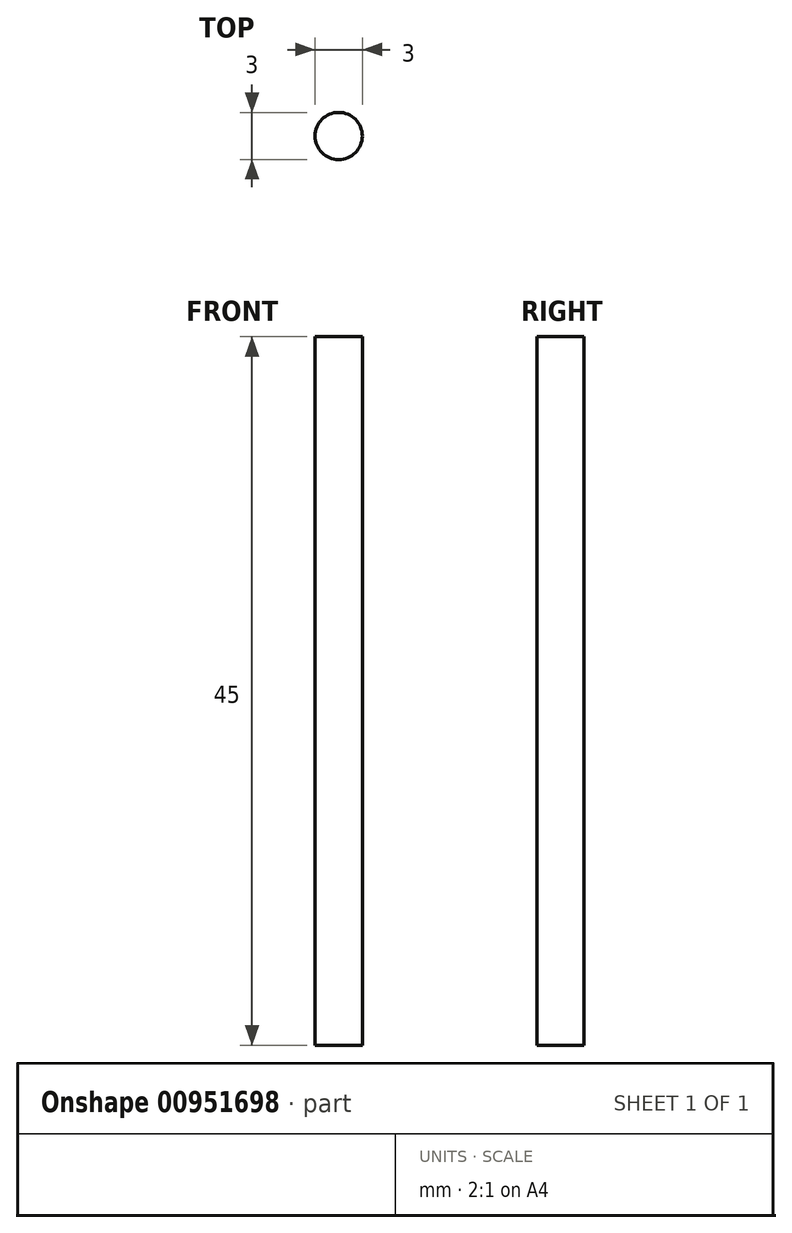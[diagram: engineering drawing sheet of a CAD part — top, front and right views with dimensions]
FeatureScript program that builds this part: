
annotation { "Feature Type Name" : "Feature", "Feature Type Description" : "" }
export const myFeature = defineFeature(function(context is Context, id is Id, definition is map)
    precondition{}
    {
        {
            var Q0;
            Q0=qCreatedBy(makeId("Top.planeOp"), FACE);
            var sketch = newSketch(context, id + "F0", { "sketchPlane" : qUnion([Q0])});
            skCircle(sketch, "E0", {"center": v(0, 0) * mm, "radius": 1.5 * mm});
            skSolve(sketch);
        }
        {
            var Q0;
            Q0 = qSketchRegion(id + "F0", true);
            extrude(context, id + "F1", {"entities" : qUnion([Q0]), "domain" : OperationDomain.MODEL, "flatOperationType" : FlatOperationType.REMOVE, "endBound" : BoundingType.SYMMETRIC, "depth" : 45 * mm, "offsetDistance" : 25 * mm});
        }
    });
